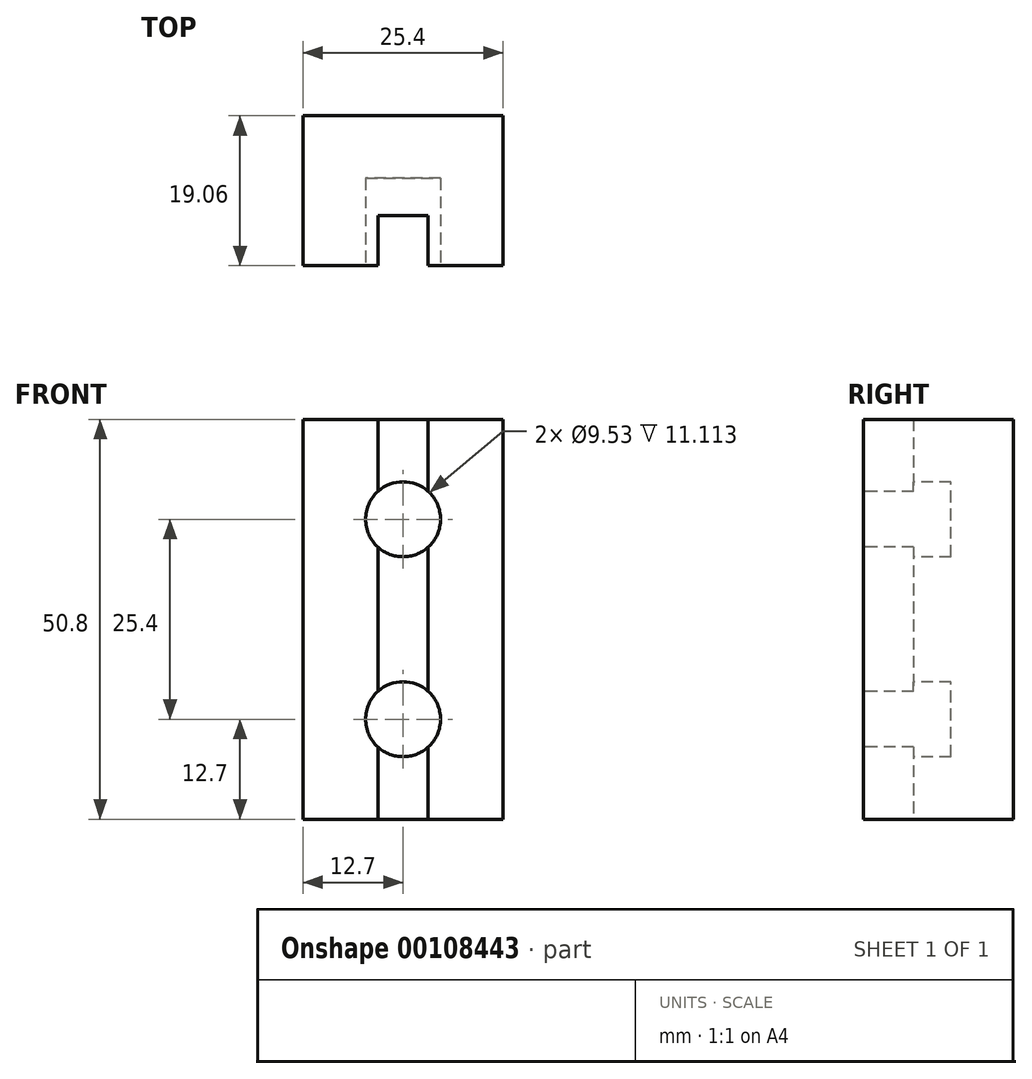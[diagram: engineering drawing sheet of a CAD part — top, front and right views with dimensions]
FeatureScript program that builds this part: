
annotation { "Feature Type Name" : "Feature", "Feature Type Description" : "" }
export const myFeature = defineFeature(function(context is Context, id is Id, definition is map)
    precondition{}
    {
        {
            var Q0;
            Q0=qCreatedBy(makeId("Top.planeOp"),FACE);
            var sketch = newSketch(context, id + "F0", { "sketchPlane" : qUnion([Q0])});
            skLineSegment(sketch, "E0.bottom", {"start": v(12.7, 9.53) * mm, "end": v(-12.7, 9.53) * mm});
            skLineSegment(sketch, "E0.top", {"start": v(12.7, -9.53) * mm, "end": v(3.18, -9.53) * mm});
            skLineSegment(sketch, "E0.left", {"start": v(12.7, 9.53) * mm, "end": v(12.7, -9.53) * mm});
            skLineSegment(sketch, "E0.right", {"start": v(-12.7, 9.53) * mm, "end": v(-12.7, -9.53) * mm});
            skPoint(sketch, "E0.middle", {"position": v(0, 0) * mm});
            skLineSegment(sketch, "E1.top", {"start": v(-3.18, -3.18) * mm, "end": v(3.17, -3.18) * mm});
            skLineSegment(sketch, "E1.left", {"start": v(-3.17, -9.53) * mm, "end": v(-3.18, -3.18) * mm});
            skLineSegment(sketch, "E1.right", {"start": v(3.18, -9.53) * mm, "end": v(3.17, -3.18) * mm});
            skLineSegment(sketch, "E2.trimOffspring", {"start": v(-3.17, -9.53) * mm, "end": v(-12.7, -9.53) * mm});
            skSolve(sketch);
        }
        {
            var Q0;
            Q0=makeQuery(id+"F0.imprint","IMPRINT",FACE,{"disambiguationData":[TD([[makeQuery(id+"F0.imprint","IMPRINT",EDGE,{"derivedFrom":sQuery(id+"F0.wireOp",EDGE,"E0.bottom")}),1.0]])]});
            extrude(context, id + "F1", {"entities" : qUnion([Q0]), "depth" : 50.8 * mm});
        }
        {
            var Q0;
            Q0=makeQuery(id+"F1.opExtrude","SWEPT_FACE",FACE,{"disambiguationData":[OSD([sQuery(id+"F0.wireOp",EDGE,"E2.trimOffspring")])]});
            var sketch = newSketch(context, id + "F2", { "sketchPlane" : qUnion([Q0])});
            skCircle(sketch, "E3", {"center": v(0, 38.1) * mm, "radius": 4.76 * mm});
            skCircle(sketch, "E4", {"center": v(0, 12.7) * mm, "radius": 4.76 * mm});
            skSolve(sketch);
        }
        {
            var Q0;
            {var subQ0=sQuery(id+"F2.wireOp",EDGE,"E3");var subQ1=makeQuery(id+"F1.opExtrude","SWEPT_EDGE",EDGE,{"disambiguationData":[OSD([sQuery(id+"F0.wireOp",EDGE,"E1.left"),sQuery(id+"F0.wireOp",EDGE,"E2.trimOffspring")])]});var subQ2=makeQuery(id+"F2.imprint","INTERSECT",VERTEX,{"disambiguationData":[OD(0.0)],"derivedFrom":[subQ1,subQ0]});Q0=makeQuery(id+"F2.imprint","IMPRINT",FACE,{"disambiguationData":[TD([[makeQuery(id+"F2.imprint","IMPRINT",EDGE,{"disambiguationData":[TD([[subQ2,1.0]])],"derivedFrom":subQ0}),1.0]])]});}
            var Q1;
            {var subQ0=sQuery(id+"F2.wireOp",EDGE,"E3");var subQ1=makeQuery(id+"F1.opExtrude","SWEPT_EDGE",EDGE,{"disambiguationData":[OSD([sQuery(id+"F0.wireOp",EDGE,"E1.left"),sQuery(id+"F0.wireOp",EDGE,"E2.trimOffspring")])]});var subQ2=makeQuery(id+"F2.imprint","INTERSECT",VERTEX,{"disambiguationData":[OD(0.0)],"derivedFrom":[subQ1,subQ0]});Q1=makeQuery(id+"F2.imprint","IMPRINT",FACE,{"disambiguationData":[TD([[makeQuery(id+"F2.imprint","IMPRINT",EDGE,{"disambiguationData":[TD([[subQ2,-1.0]])],"derivedFrom":subQ0}),1.0]])]});}
            var Q2;
            {var subQ0=sQuery(id+"F2.wireOp",EDGE,"E4");var subQ1=makeQuery(id+"F1.opExtrude","SWEPT_EDGE",EDGE,{"disambiguationData":[OSD([sQuery(id+"F0.wireOp",EDGE,"E1.left"),sQuery(id+"F0.wireOp",EDGE,"E2.trimOffspring")])]});var subQ2=makeQuery(id+"F2.imprint","INTERSECT",VERTEX,{"disambiguationData":[OD(0.0)],"derivedFrom":[subQ1,subQ0]});Q2=makeQuery(id+"F2.imprint","IMPRINT",FACE,{"disambiguationData":[TD([[makeQuery(id+"F2.imprint","IMPRINT",EDGE,{"disambiguationData":[TD([[subQ2,-1.0]])],"derivedFrom":subQ0}),1.0]])]});}
            var Q3;
            {var subQ0=sQuery(id+"F2.wireOp",EDGE,"E4");var subQ1=makeQuery(id+"F1.opExtrude","SWEPT_EDGE",EDGE,{"disambiguationData":[OSD([sQuery(id+"F0.wireOp",EDGE,"E1.left"),sQuery(id+"F0.wireOp",EDGE,"E2.trimOffspring")])]});var subQ2=makeQuery(id+"F2.imprint","INTERSECT",VERTEX,{"disambiguationData":[OD(0.0)],"derivedFrom":[subQ1,subQ0]});Q3=makeQuery(id+"F2.imprint","IMPRINT",FACE,{"disambiguationData":[TD([[makeQuery(id+"F2.imprint","IMPRINT",EDGE,{"disambiguationData":[TD([[subQ2,1.0]])],"derivedFrom":subQ0}),1.0]])]});}
            extrude(context, id + "F3", {"entities" : qUnion([Q0, Q1, Q2, Q3]), "operationType" : NewBodyOperationType.REMOVE, "oppositeDirection" : true, "depth" : 11.1 * mm});
        }
    });
